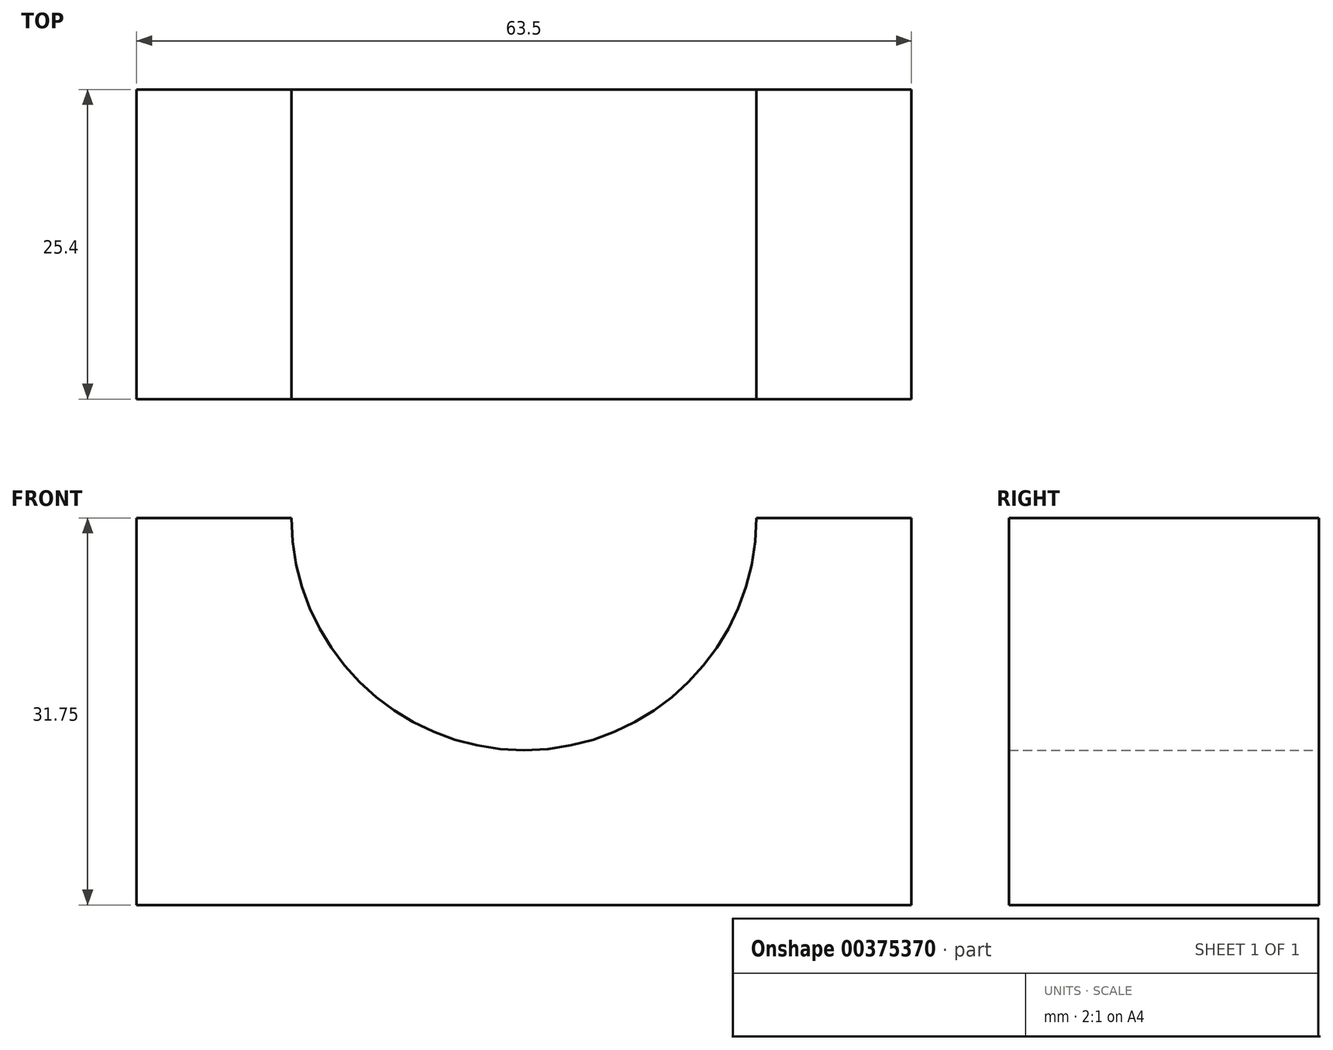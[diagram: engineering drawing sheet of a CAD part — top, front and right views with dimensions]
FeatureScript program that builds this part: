
annotation { "Feature Type Name" : "Feature", "Feature Type Description" : "" }
export const myFeature = defineFeature(function(context is Context, id is Id, definition is map)
    precondition{}
    {
        {
            var Q0;
            Q0=qCreatedBy(makeId("Front.planeOp"),FACE);
            var sketch = newSketch(context, id + "F0", { "sketchPlane" : qUnion([Q0])});
            skLineSegment(sketch, "E0", {"start": v(0, 0) * mm, "end": v(0, 31.75) * mm});
            skLineSegment(sketch, "E1", {"start": v(0, 31.75) * mm, "end": v(12.7, 31.75) * mm});
            skLineSegment(sketch, "E2", {"start": v(0, 0) * mm, "end": v(63.5, 0) * mm});
            skLineSegment(sketch, "E3", {"start": v(63.5, 0) * mm, "end": v(63.5, 31.75) * mm});
            skLineSegment(sketch, "E4", {"start": v(63.5, 31.75) * mm, "end": v(50.8, 31.75) * mm});
            skArc(sketch, "E5", {"start": v(12.7, 31.75) * mm, "mid": v(31.75, 12.7) * mm, "end": v(50.8, 31.75) * mm});
            skSolve(sketch);
        }
        {
            var Q0;
            Q0=makeQuery(id+"F0.imprint","IMPRINT",FACE,{"disambiguationData":[TD([[makeQuery(id+"F0.imprint","IMPRINT",EDGE,{"derivedFrom":sQuery(id+"F0.wireOp",EDGE,"E0")}),-1.0]])]});
            extrude(context, id + "F1", {"entities" : qUnion([Q0]), "depth" : 25.4 * mm});
        }
    });
